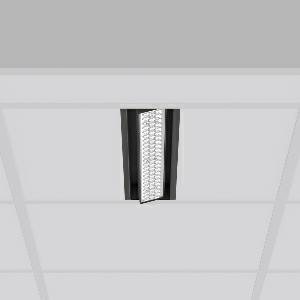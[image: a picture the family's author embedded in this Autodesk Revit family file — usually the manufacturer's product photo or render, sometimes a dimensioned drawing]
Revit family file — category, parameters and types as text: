
# Revit family: tx-move_901724_003_2_d0b6
name_source: partatom
category: Lighting Fixtures
units: mm (PartAtom-declared; Revit-internal decimal feet)

## family parameters
Cut with Voids When Loaded = No
Host = Face
Light Source = No
Part Type = Normal
Room Calculation Point = No
Round Connector Dimension = Use Diameter
Shared = No

## types (1)
- MultiLumen 1 (1 x LED Modul 927, 1950 lm, 2700)
    Apparent Load = 16 VA
    Approval mark = CE
    CIE Flux Codes = 88 96 99 100 100
    Color Rendering = 92
    Color Temperature = 2700
    Default Elevation = 1800 mm
    Description = Series: TX-MOVE
Einlege/Einbau-Flächenstrahler. Housing: sheet steel, powder-coated. Swivel range: 90°. High-efficiency LED units with optimum light control thanks to clear plastic (PC) lens optics. Spezielle Mikrostrukturen reduzieren Gelbsaum. Symmetrical light distribution. Best colour rendering with CRI >90 for fresh products and coloured textiles. Suitable for laying in grid ceiling module 600. Connected converter included in separate gearbox.Suitable for through-wiring.MultiLumen: Luminous flux adjustable in 3 steps. Accessories: Mounting frame for installation in suspended ceilings. Environmentally friendly and resource-saving due to replaceable and recyclable components. 
Colour: deep black, matt (RAL 9005)
Length: 597 mm
Width: 116 mm
Height: 39 mm
Cut-out length: 577 mm
Cut-out width: 98 mm
Recess height: 100 mm
Lamp: LED
Socket: without socket
Colour temperature: 2700K
Colour rendering index (CRI): 90
System power: 16 W
Rated luminous flux: 1950 lm
Luminous efficiency: 122 lm/W
System power 2: 23 W
Rated luminous flux 2: 2750 lm
Luminous efficiency 2: 120 lm/W
System power 3: 31 W
Rated luminous flux 3: 3500 lm
Luminous efficiency 3: 113 lm/W
Control gear: Regulated power supply
Protection class: I
Type of protection: IP 20
    Height = 0 mm  [stored 0 ft]
    Lamp = 1 x LED Modul 927
    Lamp Light Flux = 1950 lm
    Lamp count = 1
    Length = 597 mm
    Lifetime = 50000 h
    Luminous efficacy = 122 lm/W
    Manufacturer = RZB
    ModVariant = No
    Model = 901724.003.2
    Mounting Place = Ceiling, Wall
    Mounting Type = Recessed
    Number of Poles = 1
    OnlyDefault = Yes
    Power Factor = 1
    Product Name = TX-MOVE
    Product group = Recessed projectors
    ProductGroupID = 401
    Protection Class = Protection class I
    Protection Degree = IP 20
    RLX_Detail_Level = 1
    RLX_Emergency_Light_Flux = 0 lm
    RLX_Emergency_Type = 0
    RLX_Emergency_Type_DB = No
    RlxData = <blob elided: 29553 chars, md5=52073dc5>
    Socket = socket
    Standby Power = 0 W
    System Light Flux = 1950 lm
    System Power = 16 W
    Type Comments = MultiLumen 1
    Type Image = 901725.003.jpg
    URL = http://relux.com
    VarID = multilumen_1
    Voltage = 230 V
    Voltage Range = 220-240 V
    Weight = 0.00 kg
    Width = 116 mm

note: [stored X ft] marks values corroborated as IEEE doubles in the binary element streams (Revit-internal decimal feet)

## geometry (parser evidence)
native form markers: Blend x4, Sweep x12
no freeform markers — native parametric forms only
